# Revit family: Hitachi_RAF-35NXA_RAF50NXA_VER2_0813
name_source: partatom
category: Mechanical Equipment
revit_build: Autodesk Revit 2013 (Build: 20120221_2030(x64)
units: mm (PartAtom-declared; Revit-internal decimal feet)

## types (2) — shared parameters
Depth = 235 mm  [stored 0.770997 ft]
Energy Star = Yes
Height = 600 mm  [stored 1.9685 ft]
Manufacturer = Hitachi
Pip Connection Size - Liquid = 6.40 mm
Pipe Height (max.) = 10m
Pipe Length (min./max.) = 3m to 20m
URL = www.temperzone.biz
Weight (kg) = 14
Width = 760 mm

## per-type parameters (varying)
| type | Cooling Capacity | Cooling Range (kW) | Dehumidifying Capacity | Description | Heating Capacity | Heating Range (kW) | Matching Unit - Outdoor | Model - Outdoor | Pipe Connection Size - Gas |
| RAF-35NXA1 | 4 kW | 1.1 kW to 4.2 kW | 1.6 l/h | Hitachi Floor Mounted 3.5kW Heatpump RAF-35NXA1 | 4 kW | 1.1 kW to 5.2 kW | RAC-35NXA1 | RAC-35NXA1 | 9.50 mm |
| RAF-50NXA1 | 5 kW | 1.1 kW to 5.2 kW | 2.0 l/h | Hitachi Floor Mounted 5.0kW Heatpump RAF-50NXA1 | 6 kW | 2.2 kW to 7.3 kW | RAC-50NXA1 | RAC-50NXA1 | 12.70 mm |

note: column(s) folded — value = type name in every type: Model

note: [stored X ft] marks values corroborated as IEEE doubles in the binary element streams (Revit-internal decimal feet)

## geometry (parser evidence)
native form markers: Blend x4, Sweep x4
no freeform markers — native parametric forms only
